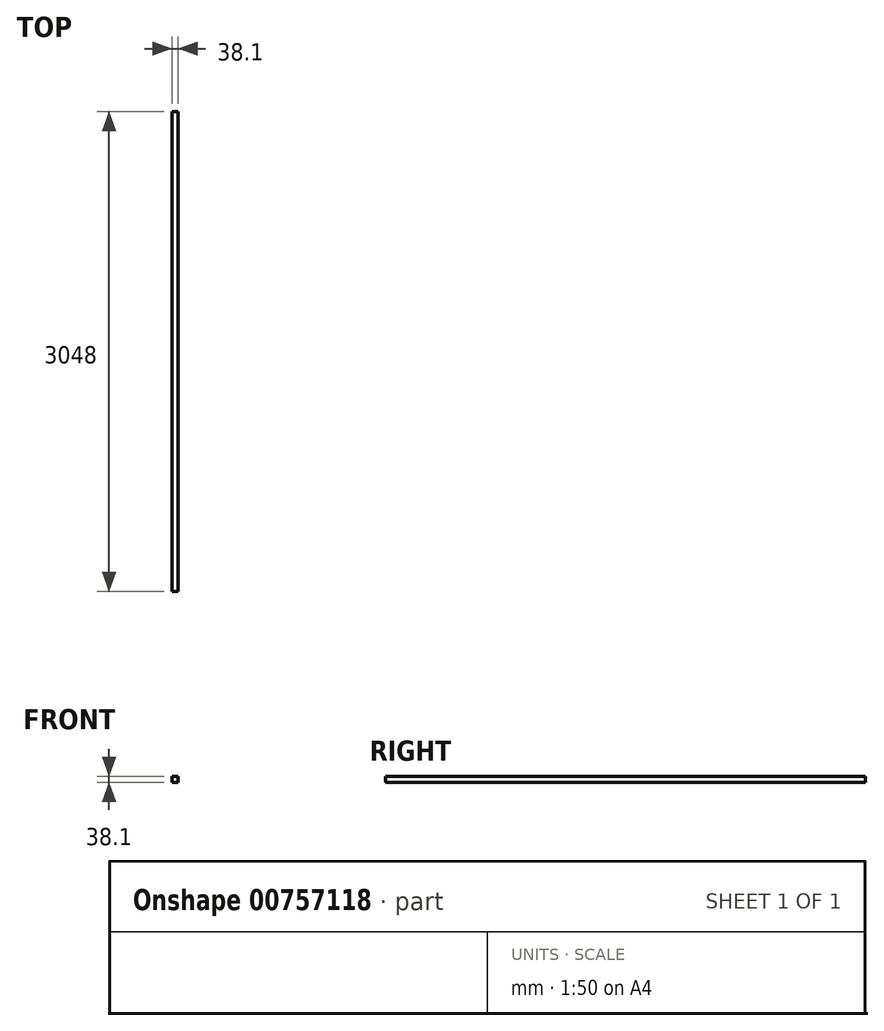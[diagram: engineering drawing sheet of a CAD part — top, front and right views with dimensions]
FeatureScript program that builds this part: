
annotation { "Feature Type Name" : "Feature", "Feature Type Description" : "" }
export const myFeature = defineFeature(function(context is Context, id is Id, definition is map)
    precondition{}
    {
        {
            var Q0;
            Q0=qCreatedBy(makeId("Front.planeOp"),FACE);
            var sketch = newSketch(context, id + "F0", { "sketchPlane" : qUnion([Q0])});
            skLineSegment(sketch, "E0.bottom", {"start": v(0, 0) * mm, "end": v(38.1, 0) * mm});
            skLineSegment(sketch, "E0.top", {"start": v(0, 38.1) * mm, "end": v(38.1, 38.1) * mm});
            skLineSegment(sketch, "E0.left", {"start": v(0, 0) * mm, "end": v(0, 38.1) * mm});
            skLineSegment(sketch, "E0.right", {"start": v(38.1, 0) * mm, "end": v(38.1, 38.1) * mm});
            skSolve(sketch);
        }
        {
            var Q0;
            Q0=makeQuery(id+"F0.imprint","IMPRINT",FACE,{"disambiguationData":[TD([[makeQuery(id+"F0.imprint","IMPRINT",EDGE,{"derivedFrom":sQuery(id+"F0.wireOp",EDGE,"E0.bottom")}),1.0]])]});
            extrude(context, id + "F1", {"entities" : qUnion([Q0]), "depth" : 3048 * mm, "offsetDistance" : 25.4 * mm});
        }
    });
